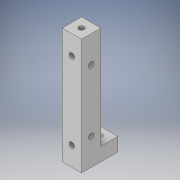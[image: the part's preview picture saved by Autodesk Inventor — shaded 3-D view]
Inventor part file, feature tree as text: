
AUTODESK INVENTOR PART (.ipt)
format: ipt  version: 2019 (Build 230136000, 136)  size: 138,752 bytes
history: native  units: mm
features: sketch x6, hole x4, extrude x2, projected_geometry x2, other x1
ambient origin geometry x8: Origin, YZ Plane, XZ Plane, XY Plane, X Axis, Y Axis, Z Axis, Center Point
bodies: Body1 (feature_tree)
feature tree (15):
  other  "Твердое тело1"
  extrude  "Выдавливание1"  Depth=10.0mm
  extrude  "Выдавливание2"  Depth=18.8mm
  hole  "Отверстие1"  [1 undecoded]
  hole  "Отверстие2"  [1 undecoded]
  hole  "Отверстие3"  [1 undecoded]
  hole  "Отверстие4"  [1 undecoded]
  sketch  "Эскиз1"
  sketch  "Эскиз2"
  sketch  "Эскиз4"
  projected_geometry  "Спроецированная петля1"
  projected_geometry  "Спроецированная петля2"
  sketch  "Эскиз7"
  sketch  "Эскиз9"
  sketch  "Эскиз11"
note: 4 required parameter values undecoded (feature->parameter linkage not recoverable at this tier; creation-order binding heuristic only, values carry confidence <= 0.55)
